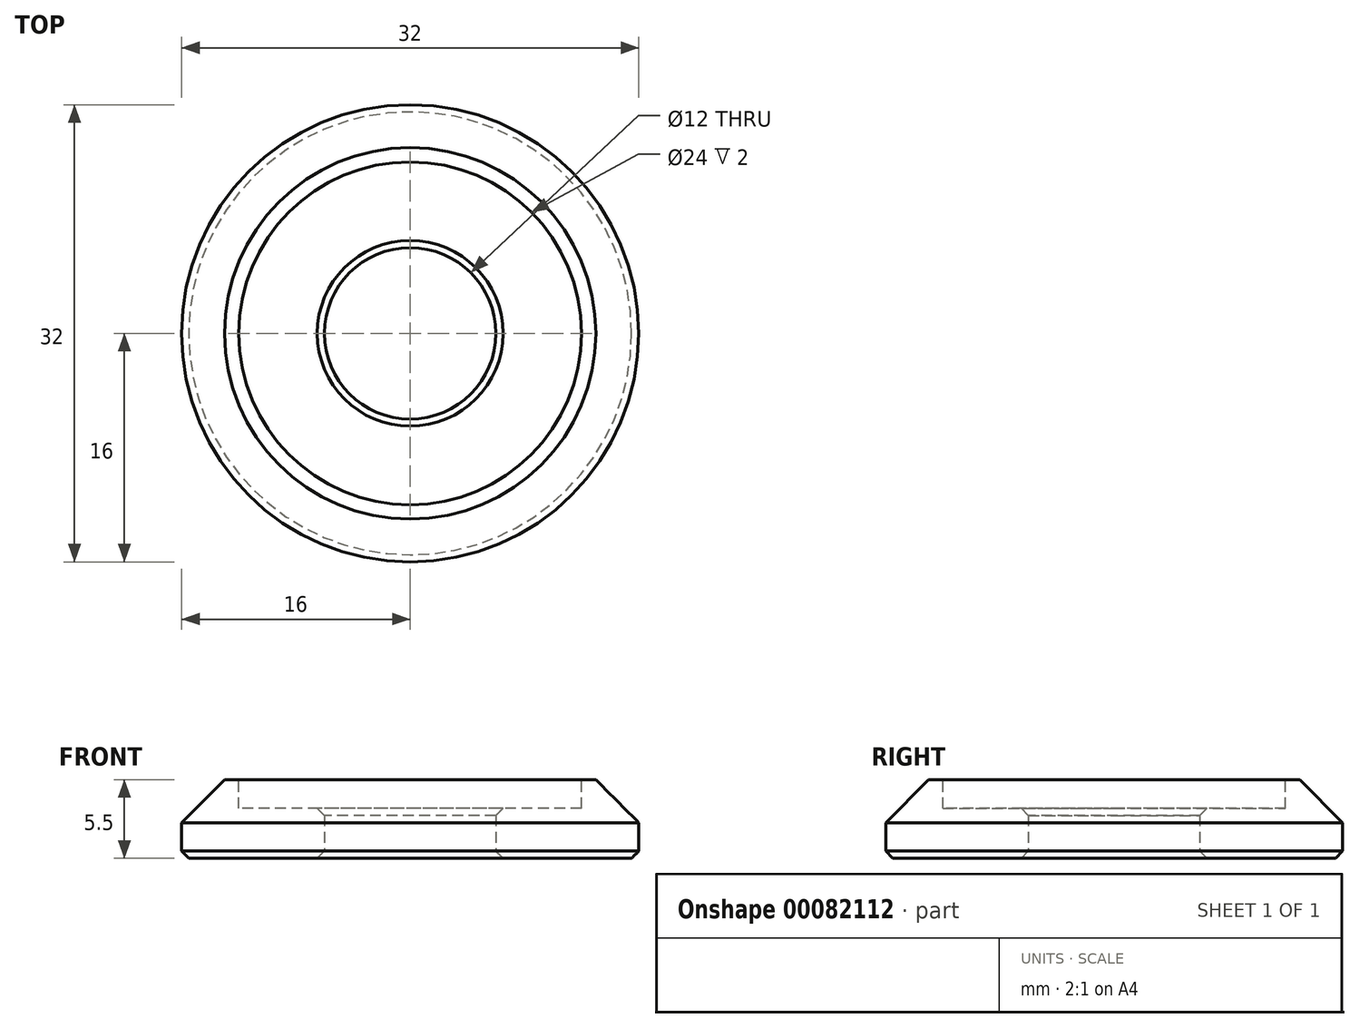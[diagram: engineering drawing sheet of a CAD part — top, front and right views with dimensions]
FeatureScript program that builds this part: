
annotation { "Feature Type Name" : "Feature", "Feature Type Description" : "" }
export const myFeature = defineFeature(function(context is Context, id is Id, definition is map)
    precondition{}
    {
        {
            var Q0;
            Q0=qCreatedBy(makeId("Top.planeOp"),FACE);
            var sketch = newSketch(context, id + "F0", { "sketchPlane" : qUnion([Q0])});
            skCircle(sketch, "E0", {"center": v(0, 0) * mm, "radius": 16 * mm});
            skCircle(sketch, "E1", {"center": v(0, 0) * mm, "radius": 6 * mm});
            skSolve(sketch);
        }
        {
            var Q0;
            Q0=makeQuery(id+"F0.imprint","IMPRINT",FACE,{"disambiguationData":[TD([[makeQuery(id+"F0.imprint","IMPRINT",EDGE,{"derivedFrom":sQuery(id+"F0.wireOp",EDGE,"E0")}),1.0]])]});
            extrude(context, id + "F1", {"entities" : qUnion([Q0]), "depth" : 5.5 * mm});
        }
        {
            var Q0;
            Q0=makeQuery(id+"F1.opExtrude","CAP_FACE",FACE,{"disambiguationData":[OSD([sQuery(id+"F0.wireOp",EDGE,"E0"),sQuery(id+"F0.wireOp",EDGE,"E1")])],"isStart":false});
            var sketch = newSketch(context, id + "F2", { "sketchPlane" : qUnion([Q0])});
            skCircle(sketch, "E2", {"center": v(0, 0) * mm, "radius": 12 * mm});
            skSolve(sketch);
        }
        {
            var Q0;
            Q0 = qSketchRegion(id + "F2", true);
            extrude(context, id + "F3", {"entities" : qUnion([Q0]), "operationType" : NewBodyOperationType.REMOVE, "oppositeDirection" : true, "depth" : 2 * mm});
        }
        {
            var Q0;
            Q0=makeQuery(id+"F1.opExtrude","CAP_EDGE",EDGE,{"disambiguationData":[OSD([sQuery(id+"F0.wireOp",EDGE,"E0")])],"isStart":false});
            chamfer(context, id + "F4", {"entities" : qUnion([Q0]), "width" : 3 * mm, "tangentPropagation" : true});
        }
        {
            var Q0;
            Q0=makeQuery(id+"F1.opExtrude","CAP_FACE",FACE,{"disambiguationData":[OSD([sQuery(id+"F0.wireOp",EDGE,"E0"),sQuery(id+"F0.wireOp",EDGE,"E1")])],"isStart":true});
            var Q1;
            Q1=makeQuery(id+"F3.boolean.opBoolean","INTERSECT",EDGE,{"derivedFrom":[makeQuery(id+"F1.opExtrude","SWEPT_FACE",FACE,{"disambiguationData":[OSD([sQuery(id+"F0.wireOp",EDGE,"E1")])]}),makeQuery(id+"F3.opExtrude","CAP_FACE",FACE,{"disambiguationData":[OSD([sQuery(id+"F2.wireOp",EDGE,"E2")])],"isStart":false})]});
            chamfer(context, id + "F5", {"entities" : qUnion([Q0, Q1]), "width" : 0.5 * mm, "tangentPropagation" : true});
        }
    });
